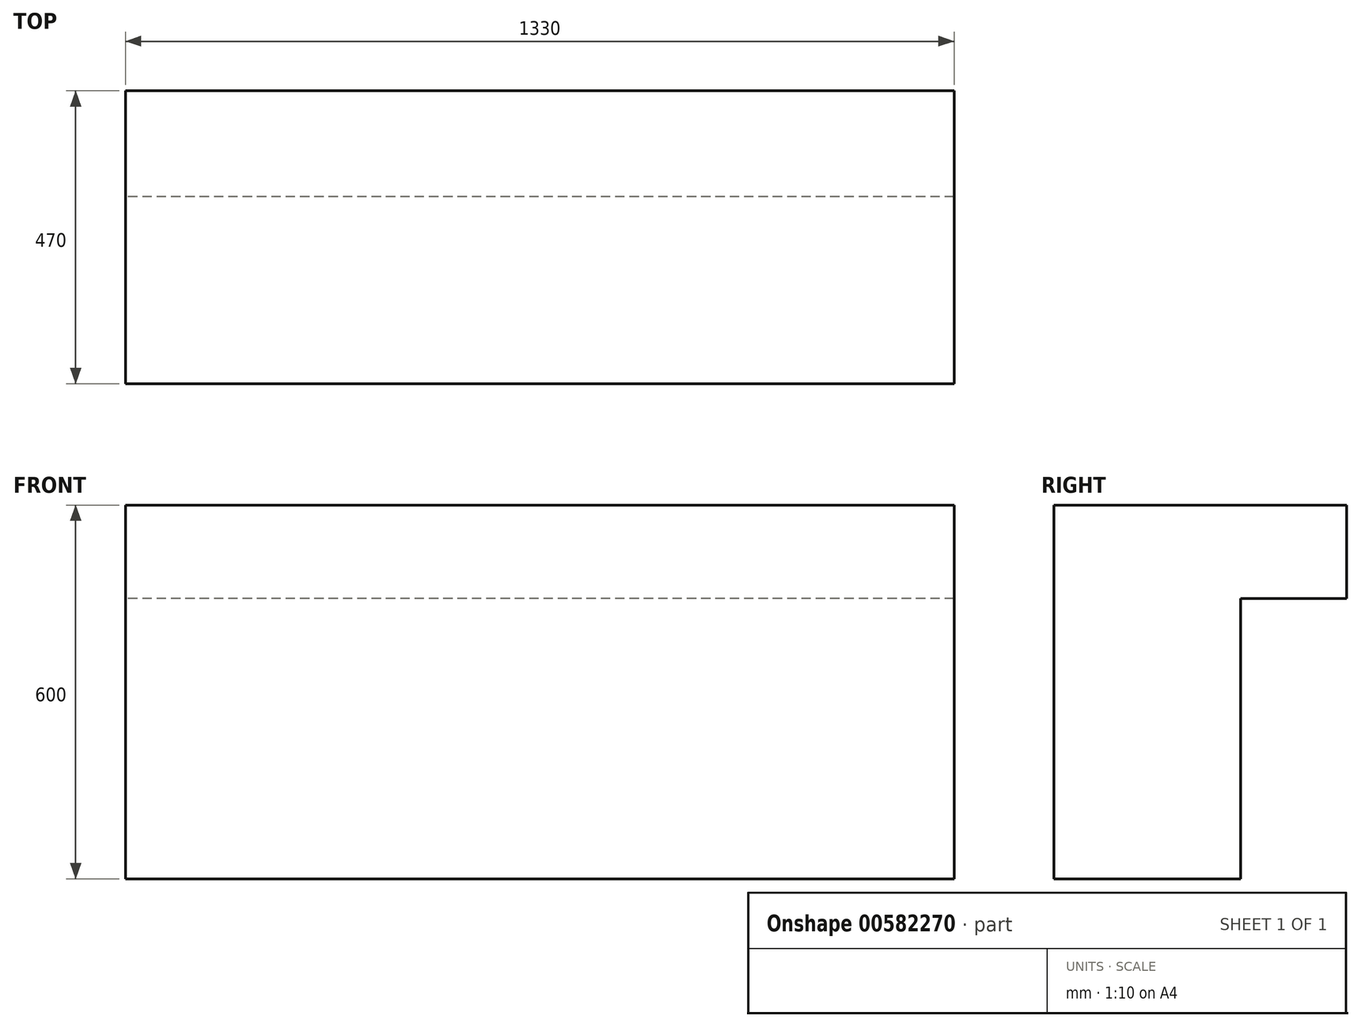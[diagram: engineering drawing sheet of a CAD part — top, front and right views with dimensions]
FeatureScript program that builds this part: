
annotation { "Feature Type Name" : "Feature", "Feature Type Description" : "" }
export const myFeature = defineFeature(function(context is Context, id is Id, definition is map)
    precondition{}
    {
        {
            var Q0;
            Q0=qCreatedBy(makeId("Right.planeOp"),FACE);
            var sketch = newSketch(context, id + "F0", { "sketchPlane" : qUnion([Q0])});
            skLineSegment(sketch, "E0.bottom", {"start": v(0, -450) * mm, "end": v(300, -450) * mm});
            skLineSegment(sketch, "E0.top", {"start": v(0, 0) * mm, "end": v(300, 0) * mm});
            skLineSegment(sketch, "E0.left", {"start": v(0, -450) * mm, "end": v(0, 0) * mm});
            skLineSegment(sketch, "E0.right", {"start": v(300, -450) * mm, "end": v(300, 0) * mm});
            skLineSegment(sketch, "E1.bottom", {"start": v(0, 0) * mm, "end": v(470, 0) * mm});
            skLineSegment(sketch, "E1.top", {"start": v(0, 150) * mm, "end": v(470, 150) * mm});
            skLineSegment(sketch, "E1.left", {"start": v(0, 0) * mm, "end": v(0, 150) * mm});
            skLineSegment(sketch, "E1.right", {"start": v(470, 0) * mm, "end": v(470, 150) * mm});
            skLineSegment(sketch, "E2.bottom", {"start": v(0, 150) * mm, "end": v(225, 150) * mm});
            skLineSegment(sketch, "E2.top", {"start": v(0, 450) * mm, "end": v(225, 450) * mm});
            skLineSegment(sketch, "E2.left", {"start": v(0, 150) * mm, "end": v(0, 450) * mm});
            skLineSegment(sketch, "E2.right", {"start": v(225, 150) * mm, "end": v(225, 450) * mm});
            skSolve(sketch);
        }
        {
            var Q0;
            Q0=makeQuery(id+"F0.imprint","IMPRINT",FACE,{"disambiguationData":[TD([[makeQuery(id+"F0.imprint","IMPRINT",EDGE,{"derivedFrom":sQuery(id+"F0.wireOp",EDGE,"E2.bottom")}),1.0]])]});
            var Q1;
            Q1=makeQuery(id+"F0.imprint","IMPRINT",FACE,{"disambiguationData":[TD([[makeQuery(id+"F0.imprint","IMPRINT",EDGE,{"derivedFrom":sQuery(id+"F0.wireOp",EDGE,"E1.top")}),-1.0]])]});
            var Q2;
            Q2=makeQuery(id+"F0.imprint","IMPRINT",FACE,{"disambiguationData":[TD([[makeQuery(id+"F0.imprint","IMPRINT",EDGE,{"derivedFrom":sQuery(id+"F0.wireOp",EDGE,"E0.bottom")}),1.0]])]});
            extrude(context, id + "F1", {"entities" : qUnion([Q0, Q1, Q2]), "endBound" : BoundingType.SYMMETRIC, "depth" : 1330 * mm, "offsetDistance" : 25 * mm});
        }
    });
